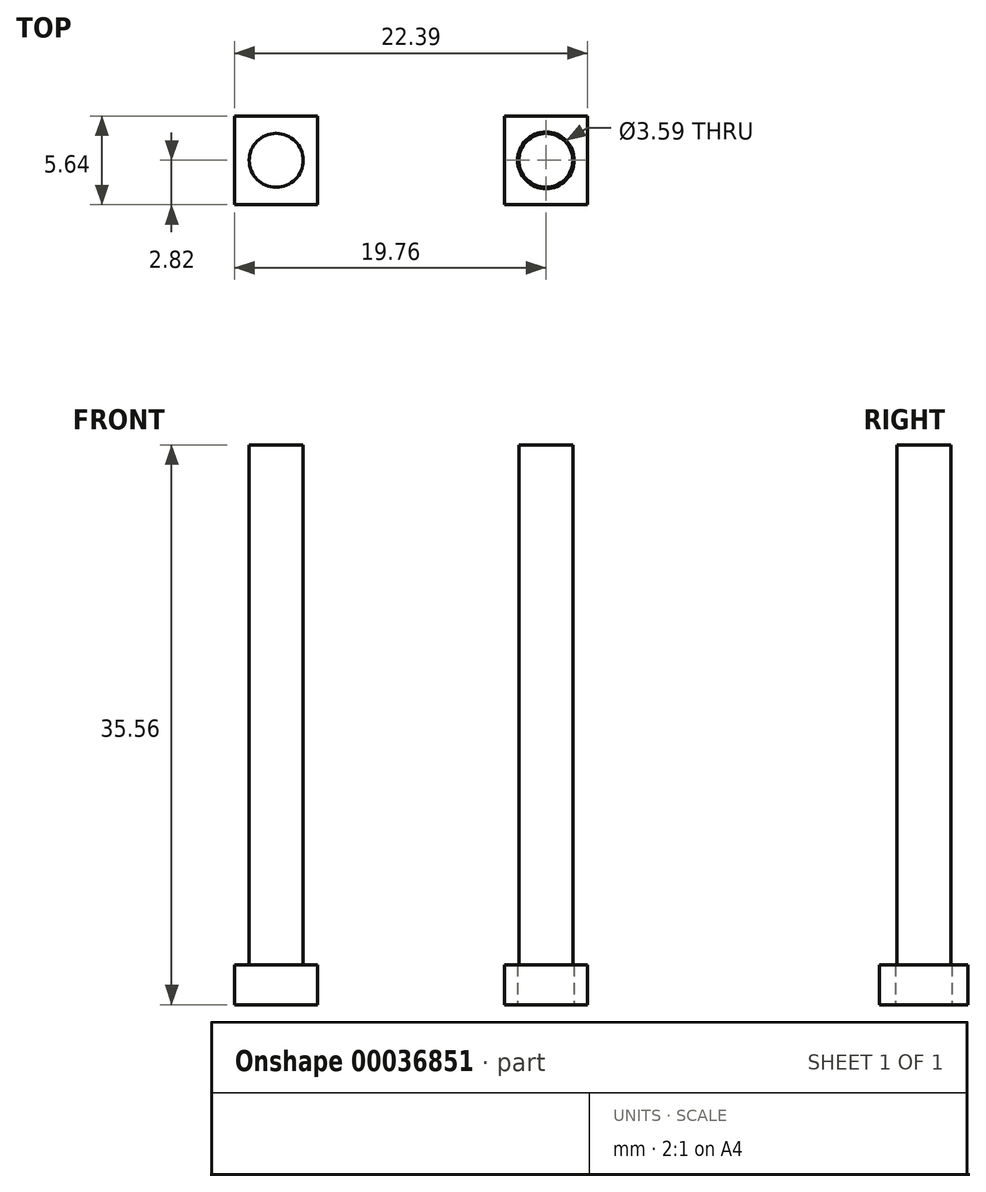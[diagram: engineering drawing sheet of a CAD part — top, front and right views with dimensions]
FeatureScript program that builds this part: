
annotation { "Feature Type Name" : "Feature", "Feature Type Description" : "" }
export const myFeature = defineFeature(function(context is Context, id is Id, definition is map)
    precondition{}
    {
        {
            var Q0;
            Q0=qCreatedBy(makeId("Top.planeOp"),FACE);
            var sketch = newSketch(context, id + "F0", { "sketchPlane" : qUnion([Q0])});
            skLineSegment(sketch, "E0.rect.bottom", {"start": v(-2.63, -2.82) * mm, "end": v(2.63, -2.82) * mm});
            skLineSegment(sketch, "E0.rect.top", {"start": v(-2.63, 2.82) * mm, "end": v(2.63, 2.82) * mm});
            skLineSegment(sketch, "E0.rect.left", {"start": v(-2.63, -2.82) * mm, "end": v(-2.63, 2.82) * mm});
            skLineSegment(sketch, "E0.rect.right", {"start": v(2.63, -2.82) * mm, "end": v(2.63, 2.82) * mm});
            skPoint(sketch, "E0.rect.middle", {"position": v(0, 0) * mm});
            skCircle(sketch, "E1", {"center": v(0, 0) * mm, "radius": 1.8 * mm});
            skLineSegment(sketch, "E2.MirrorCS", {"start": v(14.5, -2.82) * mm, "end": v(14.5, 2.82) * mm});
            skCircle(sketch, "E3.MirrorC", {"center": v(17.13, 0) * mm, "radius": 1.8 * mm});
            skLineSegment(sketch, "E4.MirrorCS", {"start": v(19.76, 2.82) * mm, "end": v(14.5, 2.82) * mm});
            skLineSegment(sketch, "E5.MirrorCS", {"start": v(19.76, -2.82) * mm, "end": v(14.5, -2.82) * mm});
            skLineSegment(sketch, "E6.MirrorCS", {"start": v(19.76, -2.82) * mm, "end": v(19.76, 2.82) * mm});
            skSolve(sketch);
        }
        {
            var Q0;
            Q0 = qSketchRegion(id + "F0", true);
            var Q1;
            Q1=makeQuery(id+"F0.imprint","IMPRINT",FACE,{"disambiguationData":[TD([[makeQuery(id+"F0.imprint","IMPRINT",EDGE,{"derivedFrom":sQuery(id+"F0.wireOp",EDGE,"E1")}),1.0]])]});
            var Q2;
            Q2=makeQuery(id+"F0.imprint","IMPRINT",FACE,{"disambiguationData":[TD([[makeQuery(id+"F0.imprint","IMPRINT",EDGE,{"derivedFrom":sQuery(id+"F0.wireOp",EDGE,"E3.MirrorC")}),-1.0]])]});
            extrude(context, id + "F1", {"entities" : qUnion([Q0, Q1, Q2]), "depth" : 2.54 * mm});
        }
        {
            var Q0;
            Q0=makeQuery(id+"F1.opExtrude","CAP_FACE",FACE,{"disambiguationData":[OSD([sQuery(id+"F0.wireOp",EDGE,"E0.rect.bottom"),sQuery(id+"F0.wireOp",EDGE,"E0.rect.top"),sQuery(id+"F0.wireOp",EDGE,"E0.rect.left"),sQuery(id+"F0.wireOp",EDGE,"E0.rect.right")])],"isStart":false});
            var sketch = newSketch(context, id + "F2", { "sketchPlane" : qUnion([Q0])});
            skCircle(sketch, "E7", {"center": v(0, 0) * mm, "radius": 1.71 * mm});
            skSolve(sketch);
        }
        {
            var Q0;
            Q0 = qSketchRegion(id + "F2", true);
            extrude(context, id + "F3", {"entities" : qUnion([Q0]), "operationType" : NewBodyOperationType.ADD, "depth" : 33.02 * mm});
        }
        {
            var Q0;
            Q0=makeQuery(id+"F1.opExtrude","CAP_FACE",FACE,{"disambiguationData":[OSD([sQuery(id+"F0.wireOp",EDGE,"E2.MirrorCS"),sQuery(id+"F0.wireOp",EDGE,"E4.MirrorCS"),sQuery(id+"F0.wireOp",EDGE,"E5.MirrorCS"),sQuery(id+"F0.wireOp",EDGE,"E6.MirrorCS")])],"isStart":false});
            var sketch = newSketch(context, id + "F4", { "sketchPlane" : qUnion([Q0])});
            skCircle(sketch, "E8", {"center": v(17.13, 0) * mm, "radius": 1.71 * mm});
            skPoint(sketch, "E9.start.orphan", {"position": v(17.13, 2.82) * mm});
            skPoint(sketch, "E10.trimOffspring.end.orphan", {"position": v(17.13, -2.82) * mm});
            skPoint(sketch, "E11.start.orphan", {"position": v(14.5, 0) * mm});
            skPoint(sketch, "E12.trimOffspring.end.orphan", {"position": v(19.76, 0) * mm});
            skSolve(sketch);
        }
        {
            var Q0;
            Q0 = qSketchRegion(id + "F4", true);
            extrude(context, id + "F5", {"entities" : qUnion([Q0]), "operationType" : NewBodyOperationType.ADD, "depth" : 33.02 * mm});
        }
    });
